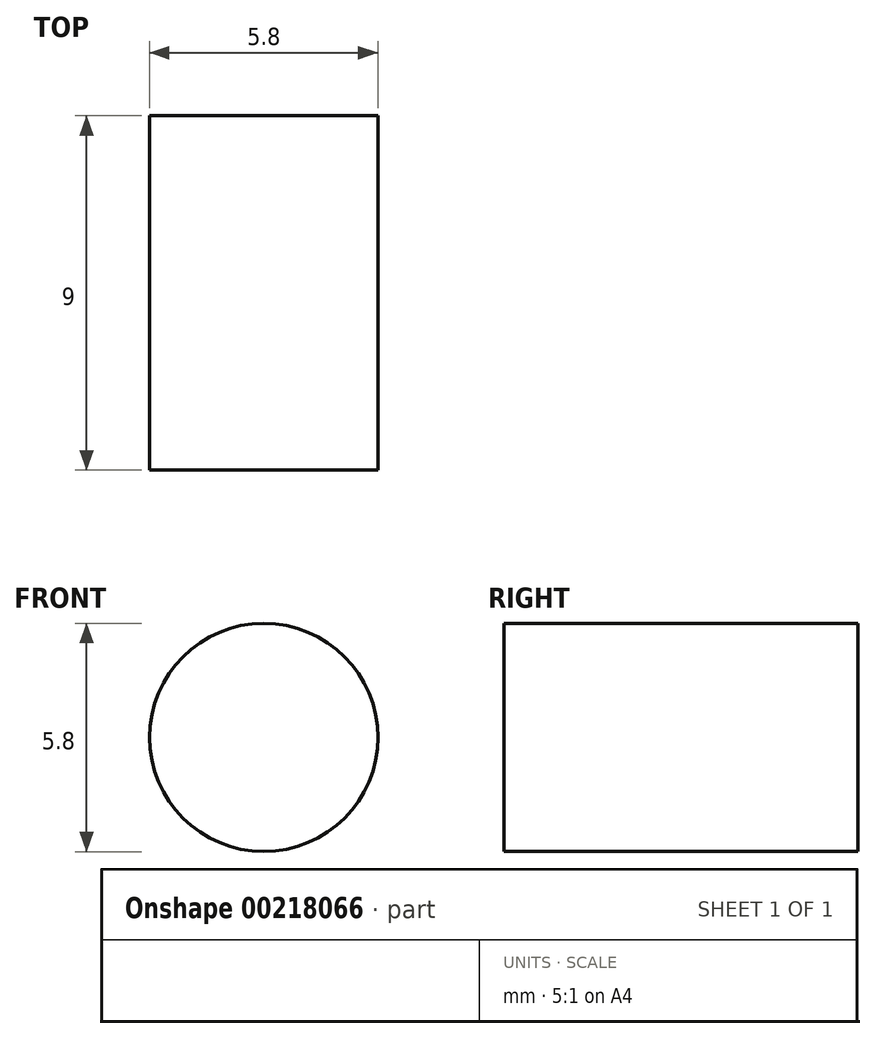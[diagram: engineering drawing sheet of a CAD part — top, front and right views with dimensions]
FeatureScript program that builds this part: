
annotation { "Feature Type Name" : "Feature", "Feature Type Description" : "" }
export const myFeature = defineFeature(function(context is Context, id is Id, definition is map)
    precondition{}
    {
        {
            var Q0;
            Q0=qCreatedBy(makeId("Front.planeOp"),FACE);
            var sketch = newSketch(context, id + "F0", { "sketchPlane" : qUnion([Q0])});
            skCircle(sketch, "E0", {"center": v(-45.17, 34.17) * mm, "radius": 2.9 * mm});
            skSolve(sketch);
        }
        {
            var Q0;
            Q0=makeQuery(id+"F0.imprint","IMPRINT",FACE,{"disambiguationData":[TD([[makeQuery(id+"F0.imprint","IMPRINT",EDGE,{"derivedFrom":sQuery(id+"F0.wireOp",EDGE,"E0")}),1.0]])]});
            extrude(context, id + "F1", {"entities" : qUnion([Q0]), "depth" : 9 * mm});
        }
    });
